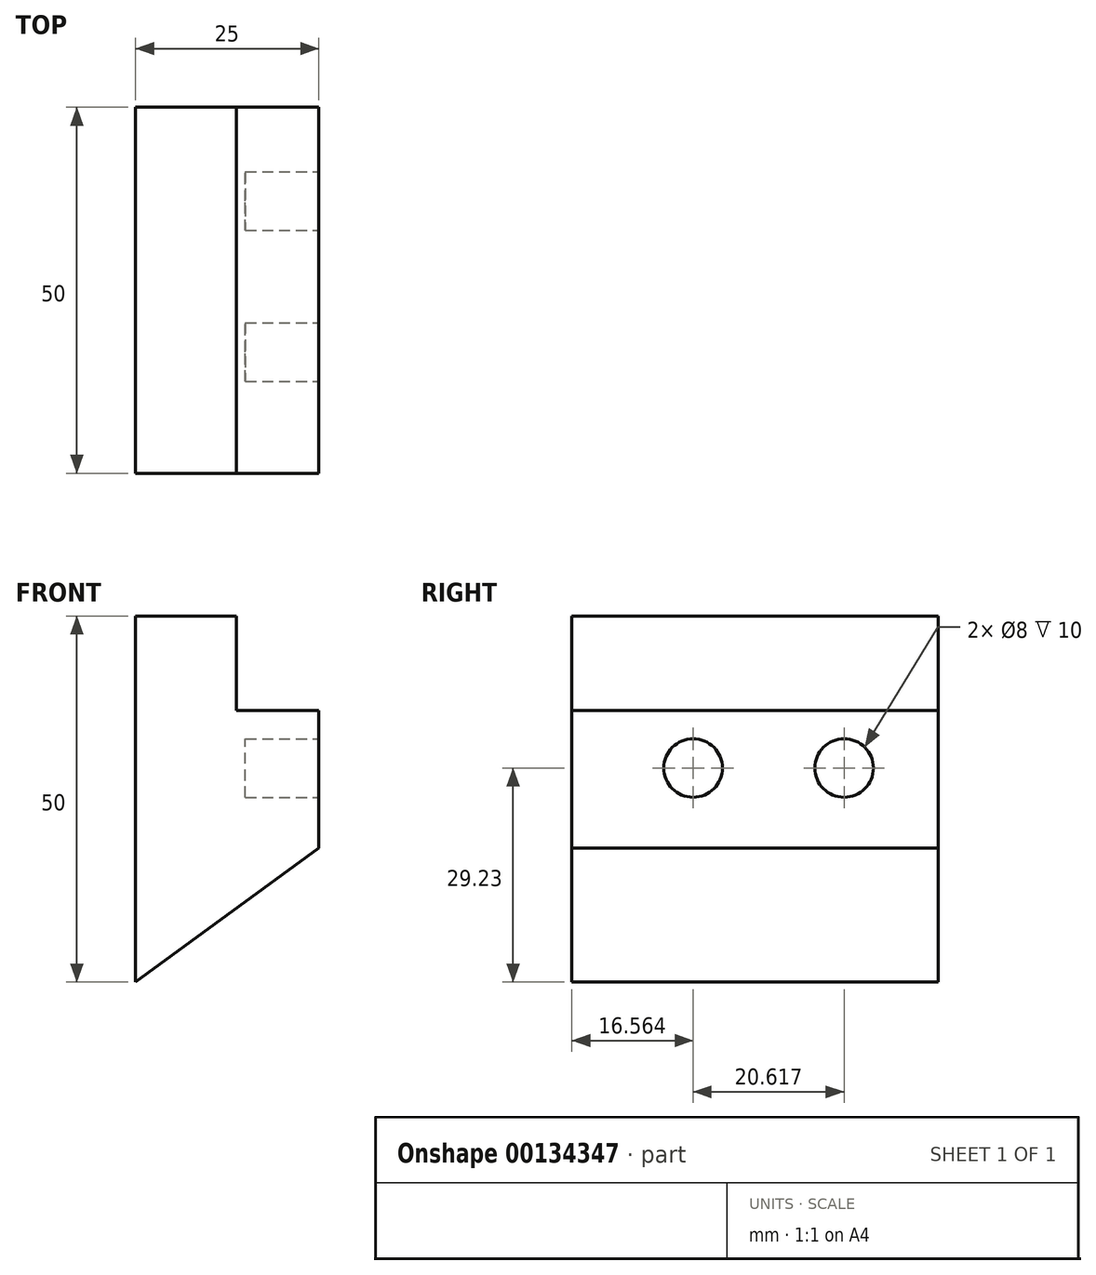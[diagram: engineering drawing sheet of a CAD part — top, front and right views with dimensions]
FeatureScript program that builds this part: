
annotation { "Feature Type Name" : "Feature", "Feature Type Description" : "" }
export const myFeature = defineFeature(function(context is Context, id is Id, definition is map)
    precondition{}
    {
        {
            var Q0;
            Q0=qCreatedBy(makeId("Front.planeOp"),FACE);
            var sketch = newSketch(context, id + "F0", { "sketchPlane" : qUnion([Q0])});
            skLineSegment(sketch, "E0.bottom", {"start": v(7.32, -13.63) * mm, "end": v(-42.68, -13.63) * mm});
            skLineSegment(sketch, "E0.top", {"start": v(7.32, 36.37) * mm, "end": v(-42.68, 36.37) * mm});
            skLineSegment(sketch, "E0.left", {"start": v(7.32, -13.63) * mm, "end": v(7.32, 36.37) * mm});
            skLineSegment(sketch, "E0.right", {"start": v(-42.68, -13.63) * mm, "end": v(-42.68, 36.37) * mm});
            skPoint(sketch, "E0.middle", {"position": v(-17.68, 11.37) * mm});
            skLineSegment(sketch, "E1", {"start": v(-6.6, 36.37) * mm, "end": v(-6.6, 23.46) * mm});
            skLineSegment(sketch, "E2", {"start": v(-6.6, 23.46) * mm, "end": v(-28.88, 23.46) * mm});
            skLineSegment(sketch, "E3", {"start": v(-28.88, 23.46) * mm, "end": v(-28.88, 36.37) * mm});
            skLineSegment(sketch, "E4", {"start": v(7.32, 4.66) * mm, "end": v(-17.68, 4.66) * mm});
            skLineSegment(sketch, "E5", {"start": v(-17.68, 4.66) * mm, "end": v(-17.68, 23.46) * mm});
            skLineSegment(sketch, "E6", {"start": v(-17.68, 4.66) * mm, "end": v(-42.68, -13.63) * mm});
            skSolve(sketch);
        }
        {
            var Q0;
            {var subQ1=sQuery(id+"F0.wireOp",EDGE,"E0.right");Q0=makeQuery(id+"F0.imprint","IMPRINT",FACE,{"disambiguationData":[TD([[makeQuery(id+"F0.imprint","IMPRINT",EDGE,{"derivedFrom":subQ1}),-1.0]])]});}
            extrude(context, id + "F1", {"entities" : qUnion([Q0]), "depth" : 50 * mm});
        }
        {
            var Q0;
            Q0=makeQuery(id+"F1.opExtrude","SWEPT_FACE",FACE,{"disambiguationData":[OSD([sQuery(id+"F0.wireOp",EDGE,"E5")])]});
            var sketch = newSketch(context, id + "F2", { "sketchPlane" : qUnion([Q0])});
            skCircle(sketch, "E7", {"center": v(-33.44, 15.6) * mm, "radius": 4 * mm});
            skCircle(sketch, "E8", {"center": v(-12.82, 15.6) * mm, "radius": 4 * mm});
            skSolve(sketch);
        }
        {
            var Q0;
            Q0=makeQuery(id+"F2.imprint","IMPRINT",FACE,{"disambiguationData":[TD([[makeQuery(id+"F2.imprint","IMPRINT",EDGE,{"derivedFrom":sQuery(id+"F2.wireOp",EDGE,"E7")}),1.0]])]});
            var Q1;
            Q1=makeQuery(id+"F2.imprint","IMPRINT",FACE,{"disambiguationData":[TD([[makeQuery(id+"F2.imprint","IMPRINT",EDGE,{"derivedFrom":sQuery(id+"F2.wireOp",EDGE,"E8")}),1.0]])]});
            extrude(context, id + "F3", {"entities" : qUnion([Q0, Q1]), "operationType" : NewBodyOperationType.REMOVE, "oppositeDirection" : true, "depth" : 10 * mm});
        }
    });
